# Revit family: Windows_Fixed-Frames_Hajom_TypeF-Alu
name_source: partatom
category: Drzwi
revit_build: Autodesk Revit 2016 (Build: 20150220_1215(x64)
units: mm (PartAtom-declared; Revit-internal decimal feet)

## family parameters
Numer OmniClass = 23.30.10.00
Obiekt nadrzędny = Ściana
Punkt obliczania pomieszczeń = Nie
Tnij formami wycięć po wczytaniu = Nie
Tytuł OmniClass = Doors
Współdzielony = Nie
Zawsze pionowo = Tak

## types (1)
- Windows_Fixed-Frames_Hajom_TypeF-Alu
    BIMobject category = Fixed Frames
    BIMobject category code = windows-fixed
    BIMobject main category = Windows
    BIMobject main category code = windows
    Brand url = https://hajom.com
    Design country = Sweden
    Edition number = 1
    Frame Projection Ext. = 25 mm  [stored 0.082021 ft]
    Frame Projection Int. = 25 mm  [stored 0.082021 ft]
    Frame Width = 75 mm  [stored 0.246063 ft]
    Funkcja = Wewnętrzna
    Grubość = 0 mm  [stored 0 ft]
    IFC Classification = Window
    Installation instructions = http://www.hajom.com
    Konstrukcja analityczna = <None>
    Manufacturer country = Sweden
    Manufacturer name = Hajom
    Masterformat 2014 Code = 08 52 00
    Masterformat 2014 Description = Wood Windows
    Material main = Wood
    Material secondary = Glass
    OmniClass Code = 23-17 13 15 11
    OmniClass Description = Wood Fixed Windows
    Product Guid = 5083bad6-47e3-4857-bc02-264239ee6fd7
    Product SKU = TypF-Alu
    Product certification = http://www.hajom.com
    Product data url = https://bimobject.com
    Product family = Skjutdörrar
    Product group = Klassiska
    Product url = http://www.hajom.com
    QR code = http://bimobject.com
    Szerokość = 0 mm  [stored 0 ft]
    Szerokość brutto = 0 mm  [stored 0 ft]
    Technical description = http://www.hajom.com
    Uniclass 2015 Code = Pr_30_59_98_96
    Uniclass 2015 Name = Wood window units
    Uniformat II Code = B2020
    Uniformat II Description = Exterior Windows
    Wysokość = 0 mm  [stored 0 ft]
    Wysokość brutto = 0 mm  [stored 0 ft]
    Zakończenie ściany = Wg obiektu nadrzędnego

note: [stored X ft] marks values corroborated as IEEE doubles in the binary element streams (Revit-internal decimal feet)

## geometry (parser evidence)
native form markers: Blend x4, Sweep x14
no freeform markers — native parametric forms only
